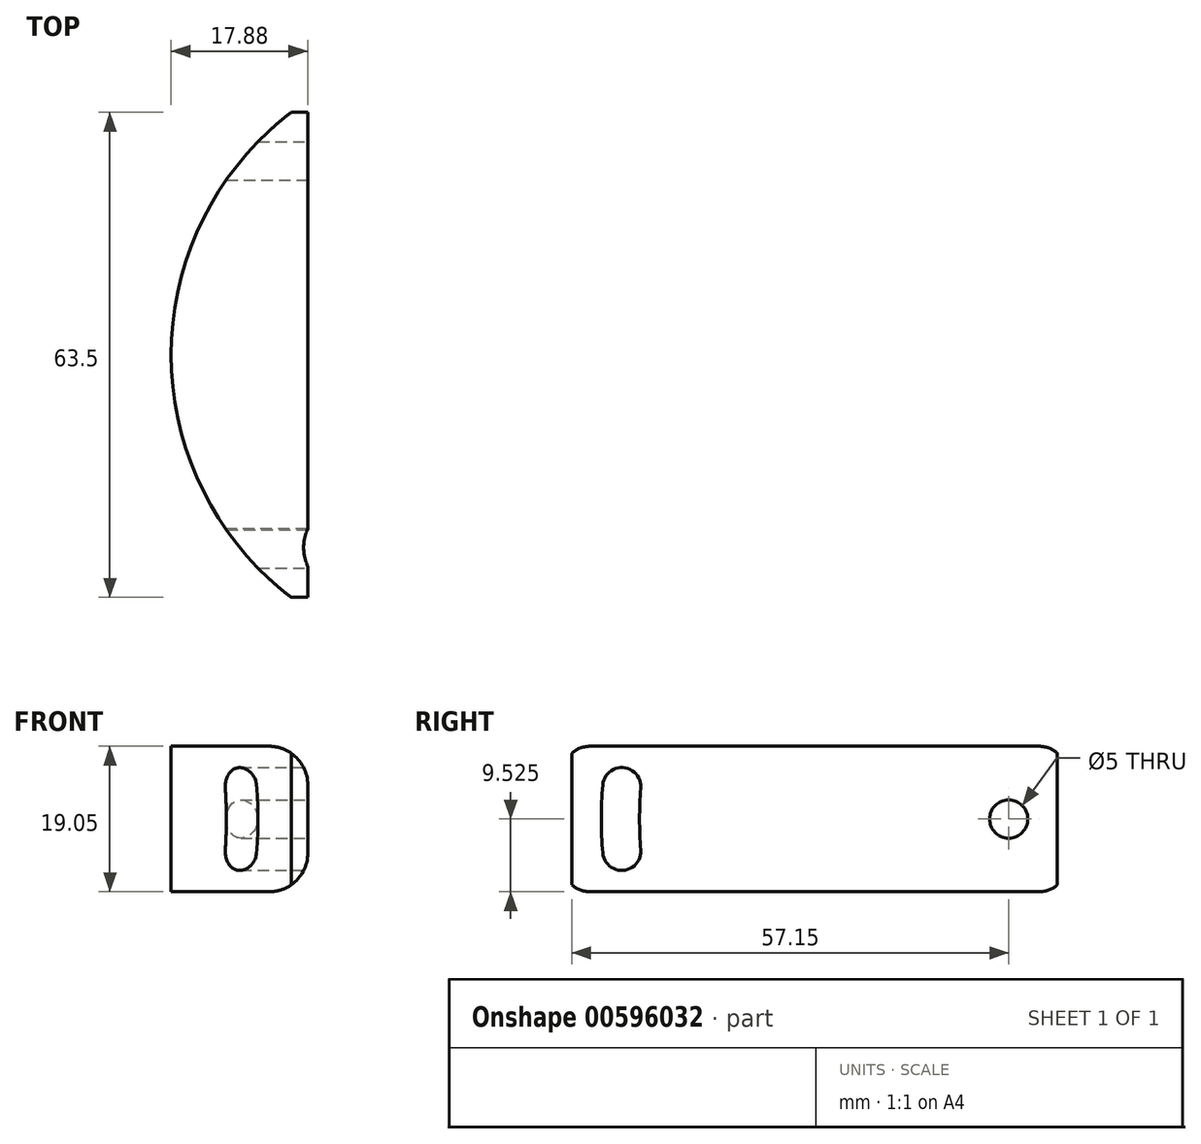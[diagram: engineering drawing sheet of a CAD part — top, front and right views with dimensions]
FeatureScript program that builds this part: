
annotation { "Feature Type Name" : "Feature", "Feature Type Description" : "" }
export const myFeature = defineFeature(function(context is Context, id is Id, definition is map)
    precondition{}
    {
        {
            var Q0;
            Q0=qCreatedBy(makeId("Top.planeOp"),FACE);
            var sketch = newSketch(context, id + "F0", { "sketchPlane" : qUnion([Q0])});
            skArc(sketch, "E0", {"start": v(-24.24, 31.75) * mm, "mid": v(-39.95, 0) * mm, "end": v(-24.24, -31.75) * mm});
            skLineSegment(sketch, "E1", {"start": v(-22.07, 31.75) * mm, "end": v(-22.07, -31.75) * mm});
            skLineSegment(sketch, "E2", {"start": v(-22.07, -31.75) * mm, "end": v(-24.24, -31.75) * mm});
            skLineSegment(sketch, "E3", {"start": v(-22.07, 31.75) * mm, "end": v(-24.24, 31.75) * mm});
            skPoint(sketch, "E4", {"position": v(-22.07, 0) * mm});
            skSolve(sketch);
        }
        {
            var Q0;
            Q0=makeQuery(id+"F0.imprint","IMPRINT",FACE,{"disambiguationData":[TD([[makeQuery(id+"F0.imprint","IMPRINT",EDGE,{"derivedFrom":sQuery(id+"F0.wireOp",EDGE,"E0")}),1.0]])]});
            extrude(context, id + "F1", {"entities" : qUnion([Q0]), "depth" : 19.05 * mm, "offsetDistance" : 25.4 * mm});
        }
        {
            var Q0;
            Q0=makeQuery(id+"F1.opExtrude","SWEPT_FACE",FACE,{"disambiguationData":[OSD([sQuery(id+"F0.wireOp",EDGE,"E1")])]});
            var sketch = newSketch(context, id + "F2", { "sketchPlane" : qUnion([Q0])});
            skLineSegment(sketch, "E5", {"start": v(-31.75, 17.15) * mm, "end": v(-31.75, 1.9) * mm});
            skPoint(sketch, "E6", {"position": v(-31.75, 9.53) * mm});
            skLineSegment(sketch, "E7", {"start": v(-31.75, 9.53) * mm, "end": v(26.83, 9.53) * mm});
            skPoint(sketch, "E8", {"position": v(-25.4, 9.53) * mm});
            skPoint(sketch, "E9", {"position": v(25.4, 9.53) * mm});
            skArc(sketch, "E10", {"start": v(-22.73, 13.55) * mm, "mid": v(-25.02, 16.25) * mm, "end": v(-27.72, 13.97) * mm});
            skArc(sketch, "E11.MirrorCS", {"start": v(-22.73, 5.5) * mm, "mid": v(-25.02, 2.8) * mm, "end": v(-27.72, 5.08) * mm});
            skPoint(sketch, "E12.MirrorCS.end.orphan", {"position": v(-27.88, 9.53) * mm});
            skPoint(sketch, "E12.MirrorCS.start.orphan", {"position": v(-44.28, 25.45) * mm});
            skPoint(sketch, "E13.MirrorCS.end.orphan", {"position": v(-22.88, 9.53) * mm});
            skPoint(sketch, "E13.MirrorCS.start.orphan", {"position": v(-22.73, 5.5) * mm});
            skArc(sketch, "E14", {"start": v(-22.73, 13.55) * mm, "mid": v(-22.9, 9.53) * mm, "end": v(-22.73, 5.5) * mm});
            skArc(sketch, "E15", {"start": v(-27.72, 13.97) * mm, "mid": v(-27.9, 9.53) * mm, "end": v(-27.72, 5.08) * mm});
            skSolve(sketch);
        }
        {
            var Q0;
            Q0=qSketchRegion(id+"F2",true);
            extrude(context, id + "F3", {"entities" : qUnion([Q0]), "operationType" : NewBodyOperationType.REMOVE, "oppositeDirection" : true, "depth" : 25.4 * mm, "offsetDistance" : 25.4 * mm});
        }
        {
            var Q0;
            Q0=sQuery(id+"F2.wireOp",VERTEX,"E9");
            var Q1;
            Q1=makeQuery(id+"F1.opExtrude","SWEPT_BODY",BODY,{"disambiguationData":[OSD([sQuery(id+"F0.wireOp",EDGE,"E0"),sQuery(id+"F0.wireOp",EDGE,"E1"),sQuery(id+"F0.wireOp",EDGE,"E2"),sQuery(id+"F0.wireOp",EDGE,"E3")])]});
            hole(context, id + "F4", {"style" : HoleStyle.SIMPLE, "endStyle" : HoleEndStyle.BLIND, "standardTappedOrClearance" : lookupTablePath({ "standard" : "ISO", "engagement" : "75%", "pitch" : "1 mm", "size" : "M6", "type" : "Tapped" }), "standardBlindInLast" : lookupTablePath({ "standard" : "ISO", "engagement" : "75%", "pitch" : "1 mm", "size" : "M6", "type" : "Tapped" }), "holeDiameter" : 5 * mm, "showTappedDepth" : true, "holeDepth" : 15.7 * mm, "isTappedThrough" : true, "tappedDepth" : 12.7 * mm, "tapClearance" : 3, "locations" : qUnion([Q0]), "scope" : qUnion([Q1]), "majorDiameter" : 6 * mm});
        }
        {
            var Q0;
            Q0=makeQuery(id+"F1.opExtrude","CAP_EDGE",EDGE,{"disambiguationData":[OSD([sQuery(id+"F0.wireOp",EDGE,"E1")])],"isStart":false});
            var Q1;
            Q1=makeQuery(id+"F1.opExtrude","CAP_EDGE",EDGE,{"disambiguationData":[OSD([sQuery(id+"F0.wireOp",EDGE,"E1")])],"isStart":true});
            fillet(context, id + "F5", {"entities" : qUnion([Q0, Q1]), "radius" : 5.08 * mm, "tangentPropagation" : true, "allowEdgeOverflow" : false});
        }
    });
